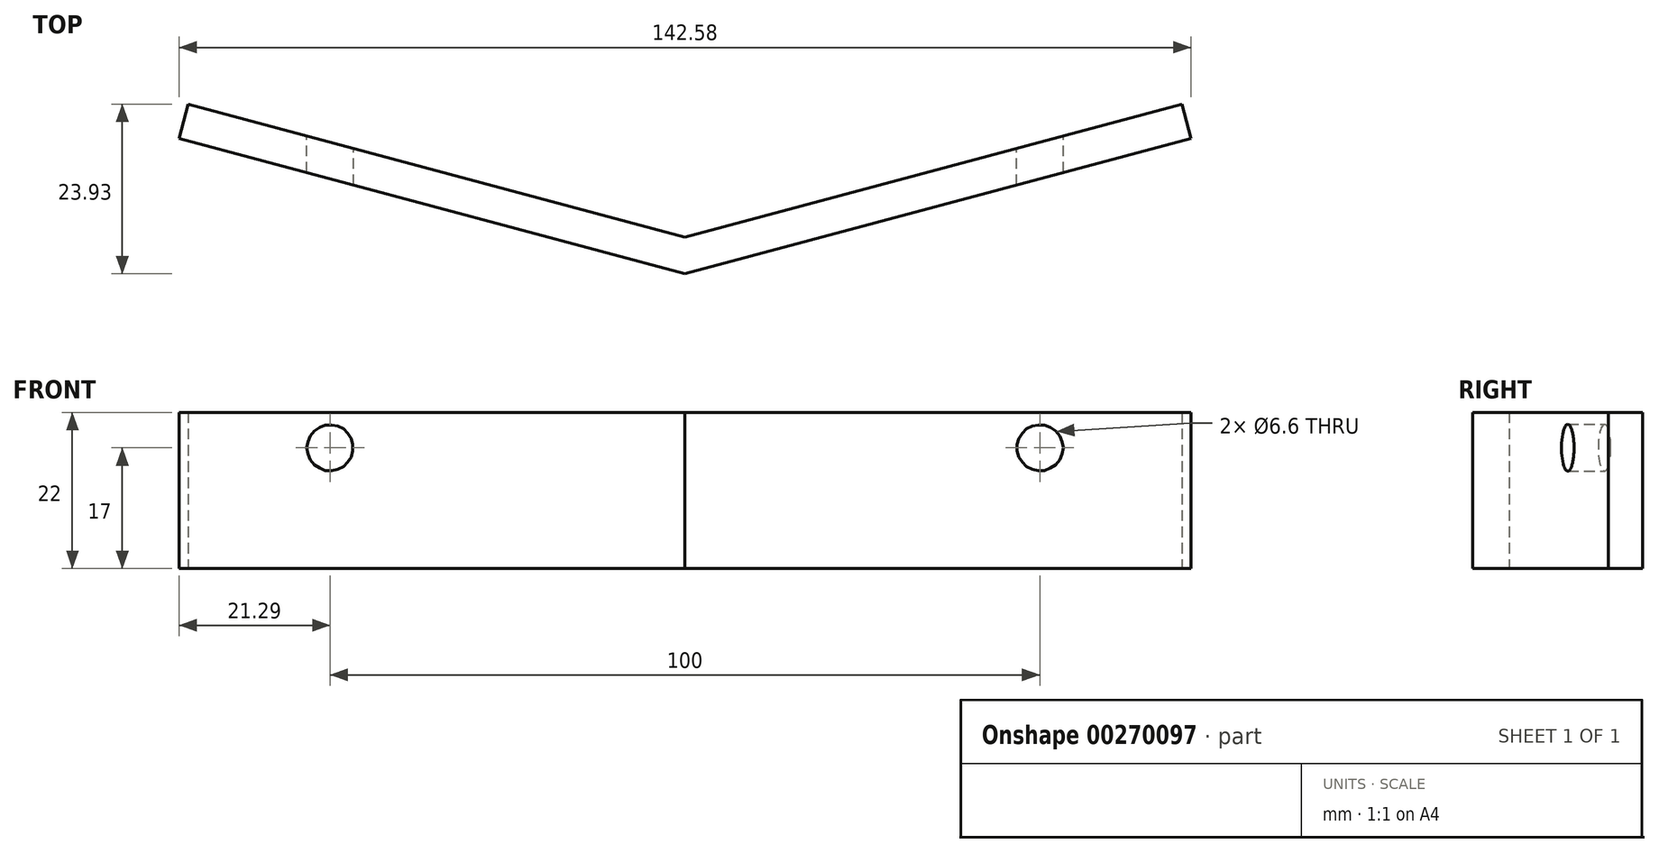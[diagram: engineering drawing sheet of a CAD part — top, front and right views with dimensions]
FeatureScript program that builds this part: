
annotation { "Feature Type Name" : "Feature", "Feature Type Description" : "" }
export const myFeature = defineFeature(function(context is Context, id is Id, definition is map)
    precondition{}
    {
        {
            var Q0;
            Q0=qCreatedBy(makeId("Top.planeOp"),FACE);
            var sketch = newSketch(context, id + "F0", { "sketchPlane" : qUnion([Q0])});
            skLineSegment(sketch, "E0", {"start": v(-88.39, 0) * mm, "end": v(105.8, 0) * mm, "construction": true});
            skLineSegment(sketch, "E1", {"start": v(-71.3, 19.1) * mm, "end": v(0, 0) * mm});
            skLineSegment(sketch, "E2", {"start": v(0, 0) * mm, "end": v(71.3, 19.1) * mm});
            skLineSegment(sketch, "E3.0", {"start": v(0, 5.18) * mm, "end": v(70, 23.93) * mm});
            skLineSegment(sketch, "E3.1", {"start": v(-70, 23.93) * mm, "end": v(0, 5.18) * mm});
            skLineSegment(sketch, "E4", {"start": v(-71.3, 19.1) * mm, "end": v(-70, 23.93) * mm});
            skLineSegment(sketch, "E5", {"start": v(71.3, 19.1) * mm, "end": v(70, 23.93) * mm});
            skSolve(sketch);
        }
        {
            var Q0;
            Q0=makeQuery(id+"F0.imprint","IMPRINT",FACE,{"disambiguationData":[TD([[makeQuery(id+"F0.imprint","IMPRINT",EDGE,{"derivedFrom":sQuery(id+"F0.wireOp",EDGE,"E1")}),1.0]])]});
            extrude(context, id + "F1", {"entities" : qUnion([Q0]), "depth" : 22 * mm});
        }
        {
            var Q0;
            Q0=qCreatedBy(makeId("Front.planeOp"),FACE);
            var sketch = newSketch(context, id + "F2", { "sketchPlane" : qUnion([Q0])});
            skPoint(sketch, "E6", {"position": v(-50, 17) * mm});
            skPoint(sketch, "E7", {"position": v(50, 17) * mm});
            skSolve(sketch);
        }
        {
            var Q0;
            Q0=sQuery(id+"F2.wireOp",VERTEX,"E6");
            var Q1;
            Q1=sQuery(id+"F2.wireOp",VERTEX,"E7");
            var Q2;
            Q2=makeQuery(id+"F1.opExtrude","SWEPT_BODY",BODY,{"disambiguationData":[OSD([sQuery(id+"F0.wireOp",EDGE,"E1"),sQuery(id+"F0.wireOp",EDGE,"E2"),sQuery(id+"F0.wireOp",EDGE,"E3.0"),sQuery(id+"F0.wireOp",EDGE,"E3.1"),sQuery(id+"F0.wireOp",EDGE,"E4"),sQuery(id+"F0.wireOp",EDGE,"E5")])]});
            hole(context, id + "F3", {"style" : HoleStyle.SIMPLE, "endStyle" : HoleEndStyle.THROUGH, "standardTappedOrClearance" : lookupTablePath({ "standard" : "ISO", "fit" : "Normal", "size" : "M6", "type" : "Clearance" }), "standardBlindInLast" : lookupTablePath({ "fit" : "Standard", "standard" : "ISO", "size" : "M6", "type" : "Clearance" }), "holeDiameter" : 6.6 * mm, "tappedDepth" : 12 * mm, "tapClearance" : 3, "startFromSketch" : true, "locations" : qUnion([Q0, Q1]), "scope" : qUnion([Q2])});
        }
    });
